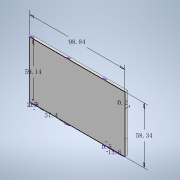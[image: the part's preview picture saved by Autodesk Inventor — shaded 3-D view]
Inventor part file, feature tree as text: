
AUTODESK INVENTOR PART (.ipt)
format: ipt  version: 2022 (Build 260153000, 153)  size: 258,560 bytes
history: native  units: mm
features: other x14, extrude x4, sketch x1
ambient origin geometry x8: Origin, YZ Plane, XZ Plane, XY Plane, X Axis, Y Axis, Z Axis, Center Point
bodies: 实体1 (feature_tree), 实体2 (feature_tree), 实体3 (feature_tree), 实体4 (feature_tree), 实体5 (feature_tree), 实体6 (feature_tree), 实体7 (feature_tree), 实体8 (feature_tree), 实体9 (feature_tree), 实体10 (feature_tree), 实体11 (feature_tree), 实体12 (feature_tree), 实体13 (feature_tree), 实体14 (feature_tree), 实体15 (feature_tree)
feature tree (19):
  sketch  "草图1"  dims[d0=98.84mm d1=58.34mm d2=2.5mm d3=0.8mm d4=30.0mm d6=37.4mm d7=20.0mm d9=59.14mm d12=15.6mm d13=0.5mm d14=2.72mm d15=0.0mm d16=0.8mm d17=0.0mm d18=0.1mm d19=0.0mm d20=0.24mm d21=0.24mm d22=0.24mm d23=2.62mm d24=0.24mm d25=0.24mm d26=0.24mm d27=0.2mm d28=2.72mm d29=0.0mm]
  extrude  "拉伸1"  Depth=58.34mm
  extrude  "拉伸2"  Depth=2.5mm
  extrude  "拉伸3"  Depth=0.8mm
  other  "分割1"
  other  "分割2"
  other  "分割3"
  other  "分割4"
  other  "分割5"
  other  "分割6"
  other  "分割7"
  other  "移动实体1"
  other  "移动实体2"
  other  "移动实体3"
  other  "移动实体4"
  other  "移动实体5"
  other  "移动实体6"
  other  "移动实体7"
  extrude  "拉伸4"  Depth=37.4mm
